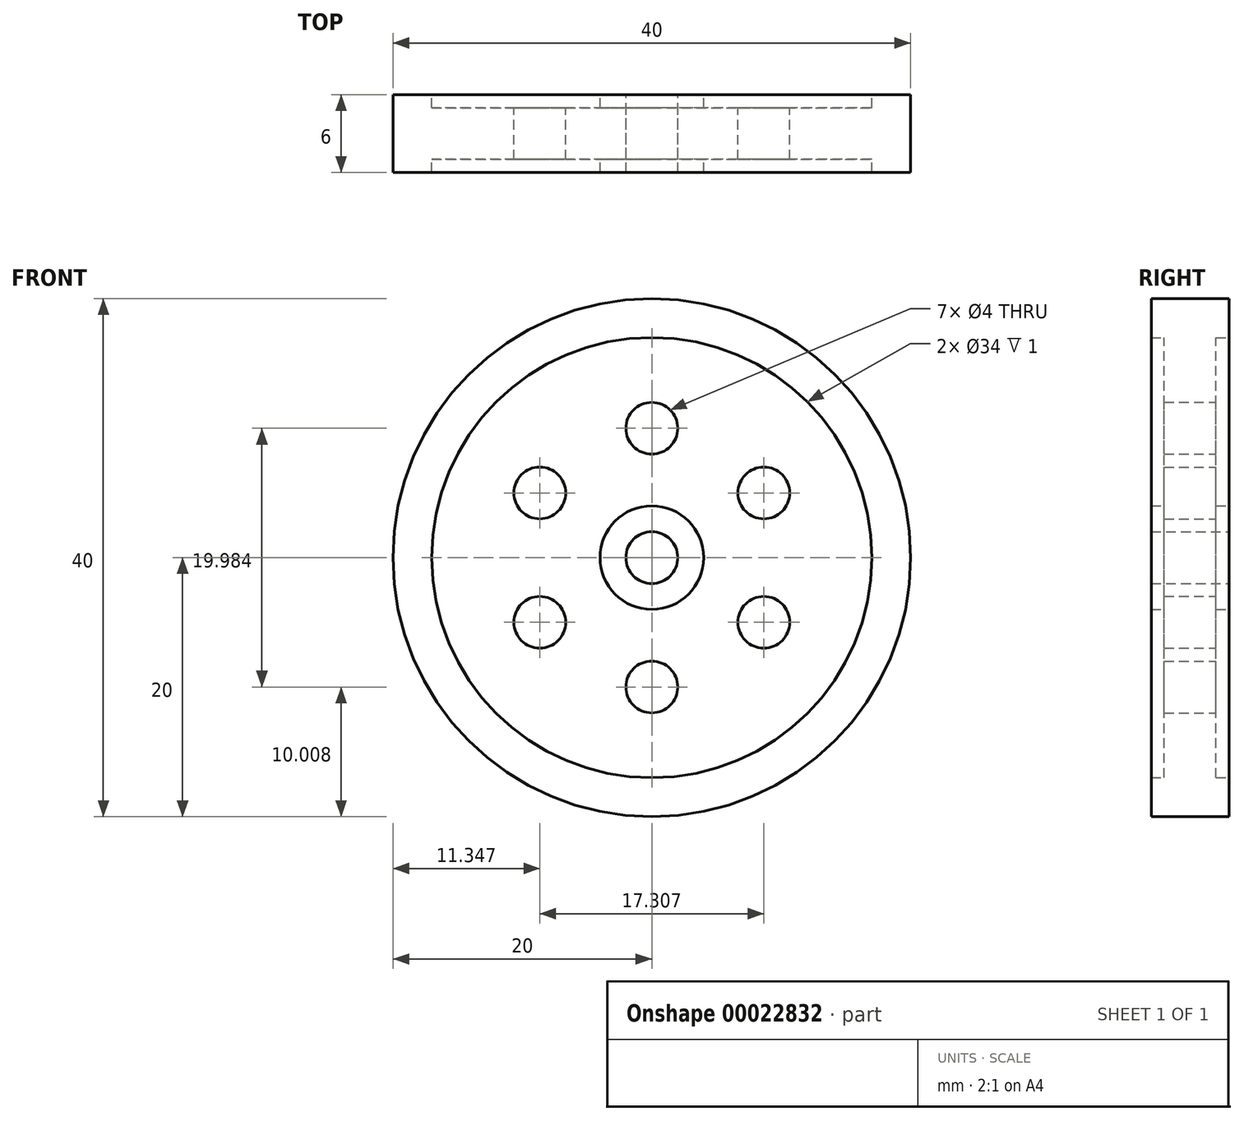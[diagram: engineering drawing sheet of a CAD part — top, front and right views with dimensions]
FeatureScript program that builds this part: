
annotation { "Feature Type Name" : "Feature", "Feature Type Description" : "" }
export const myFeature = defineFeature(function(context is Context, id is Id, definition is map)
    precondition{}
    {
        {
            var Q0;
            Q0=qCreatedBy(makeId("Front.planeOp"),FACE);
            var sketch = newSketch(context, id + "F0", { "sketchPlane" : qUnion([Q0])});
            skCircle(sketch, "E0", {"center": v(0, 0) * mm, "radius": 20 * mm});
            skCircle(sketch, "E1", {"center": v(0, 0) * mm, "radius": 2 * mm});
            skCircle(sketch, "E2", {"center": v(0, 0) * mm, "radius": 4 * mm});
            skCircle(sketch, "E3", {"center": v(0, 10) * mm, "radius": 2 * mm});
            skCircle(sketch, "E4.1.0", {"center": v(-8.65, 5) * mm, "radius": 2 * mm});
            skCircle(sketch, "E4.2.0", {"center": v(-8.65, -5) * mm, "radius": 2 * mm});
            skCircle(sketch, "E4.3.0", {"center": v(0, -10) * mm, "radius": 2 * mm});
            skCircle(sketch, "E5.1.4.0", {"center": v(8.65, -5) * mm, "radius": 2 * mm});
            skCircle(sketch, "E5.1.5.0", {"center": v(8.65, 5) * mm, "radius": 2 * mm});
            skCircle(sketch, "E6", {"center": v(0, 0) * mm, "radius": 17 * mm});
            skLineSegment(sketch, "E7", {"start": v(0, 20) * mm, "end": v(0, 17) * mm});
            skSolve(sketch);
        }
        {
            var Q0;
            Q0=makeQuery(id+"F0.imprint","IMPRINT",FACE,{"disambiguationData":[TD([[makeQuery(id+"F0.imprint","IMPRINT",EDGE,{"derivedFrom":sQuery(id+"F0.wireOp",EDGE,"E2")}),-1.0]])]});
            extrude(context, id + "F1", {"entities" : qUnion([Q0]), "endBound" : BoundingType.SYMMETRIC, "depth" : 4 * mm});
        }
        {
            var Q0;
            Q0=makeQuery(id+"F0.imprint","IMPRINT",FACE,{"disambiguationData":[TD([[makeQuery(id+"F0.imprint","IMPRINT",EDGE,{"derivedFrom":sQuery(id+"F0.wireOp",EDGE,"E1")}),-1.0]])]});
            extrude(context, id + "F2", {"entities" : qUnion([Q0]), "operationType" : NewBodyOperationType.ADD, "endBound" : BoundingType.SYMMETRIC, "depth" : 6 * mm});
        }
        {
            var Q0;
            Q0=makeQuery(id+"F0.imprint","IMPRINT",FACE,{"disambiguationData":[TD([[makeQuery(id+"F0.imprint","IMPRINT",EDGE,{"derivedFrom":sQuery(id+"F0.wireOp",EDGE,"E0")}),1.0]])]});
            extrude(context, id + "F3", {"entities" : qUnion([Q0]), "operationType" : NewBodyOperationType.ADD, "endBound" : BoundingType.SYMMETRIC, "depth" : 6 * mm});
        }
    });
